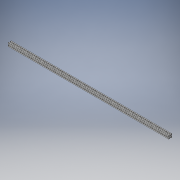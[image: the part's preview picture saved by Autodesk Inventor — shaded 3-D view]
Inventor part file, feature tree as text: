
AUTODESK INVENTOR PART (.ipt)
format: ipt  version: 2019 (Build 230136000, 136)  size: 171,520 bytes
history: native  units: in
note: dims shown in document units (in); Inventor stores cm internally (conversion verified against a paired STEP export)
features: extrude x1, fillet x1, sketch x1
ambient origin geometry x8: Origin, YZ Plane, XZ Plane, XY Plane, X Axis, Y Axis, Z Axis, Center Point
bodies: Solid1 (feature_tree)
feature tree (3):
  extrude  "Extrusion1"  Depth=0.0492in
  fillet  "Fillet1"  [1 undecoded]
  sketch  "Sketch1"  dims[d0=0.1969in d3=0.1417in d4=45.0deg d5=0.122in d7=0.2165in d8=0.063in d11=0.1693in d12=37.4016in d13=0.0in d14=0.0492in]
note: 1 required parameter value undecoded (feature->parameter linkage not recoverable at this tier; creation-order binding heuristic only, values carry confidence <= 0.55)
